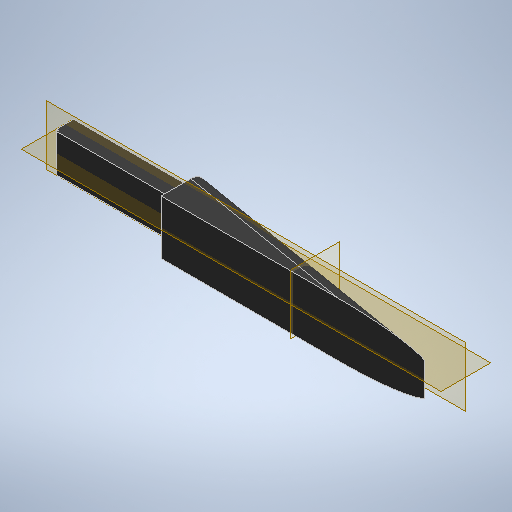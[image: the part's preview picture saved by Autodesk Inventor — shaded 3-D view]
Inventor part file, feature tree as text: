
AUTODESK INVENTOR PART (.ipt)
format: ipt  version: 2025.1 (Build 291241020, 241B)  size: 285,696 bytes
history: native  units: mm
features: extrude x4, sketch x4, fillet x1
ambient origin geometry x8: Origin, YZ Plane, XZ Plane, XY Plane, X Axis, Y Axis, Z Axis, Center Point
bodies: Solid1 (feature_tree)
feature tree (9):
  extrude  "Extrusion1"  Depth=18.0mm
  extrude  "Extrusion2"  Depth=0.25mm
  extrude  "Extrusion4"  Depth=12.5mm
  extrude  "Extrusion5"  Depth=38.75mm TaperAngle=0.0deg
  fillet  "Fillet2"  Radius=5.0mm
  sketch  "Sketch1"  dims[d0=87.5mm d1=18.0mm]
  sketch  "Sketch3"  dims[d2=15.0mm d3=0.0mm d5=0.25mm]
  sketch  "Sketch5"  dims[d6=0.0mm d7=0.0mm d14=12.5mm]
  sketch  "Sketch7"  dims[d15=5.65mm d16=38.75mm d17=0.0mm d19=5.0mm d23=98.0mm d24=175.45mm d25=5.65mm d26=0.0mm d28=3.95mm d29=4.7mm]
